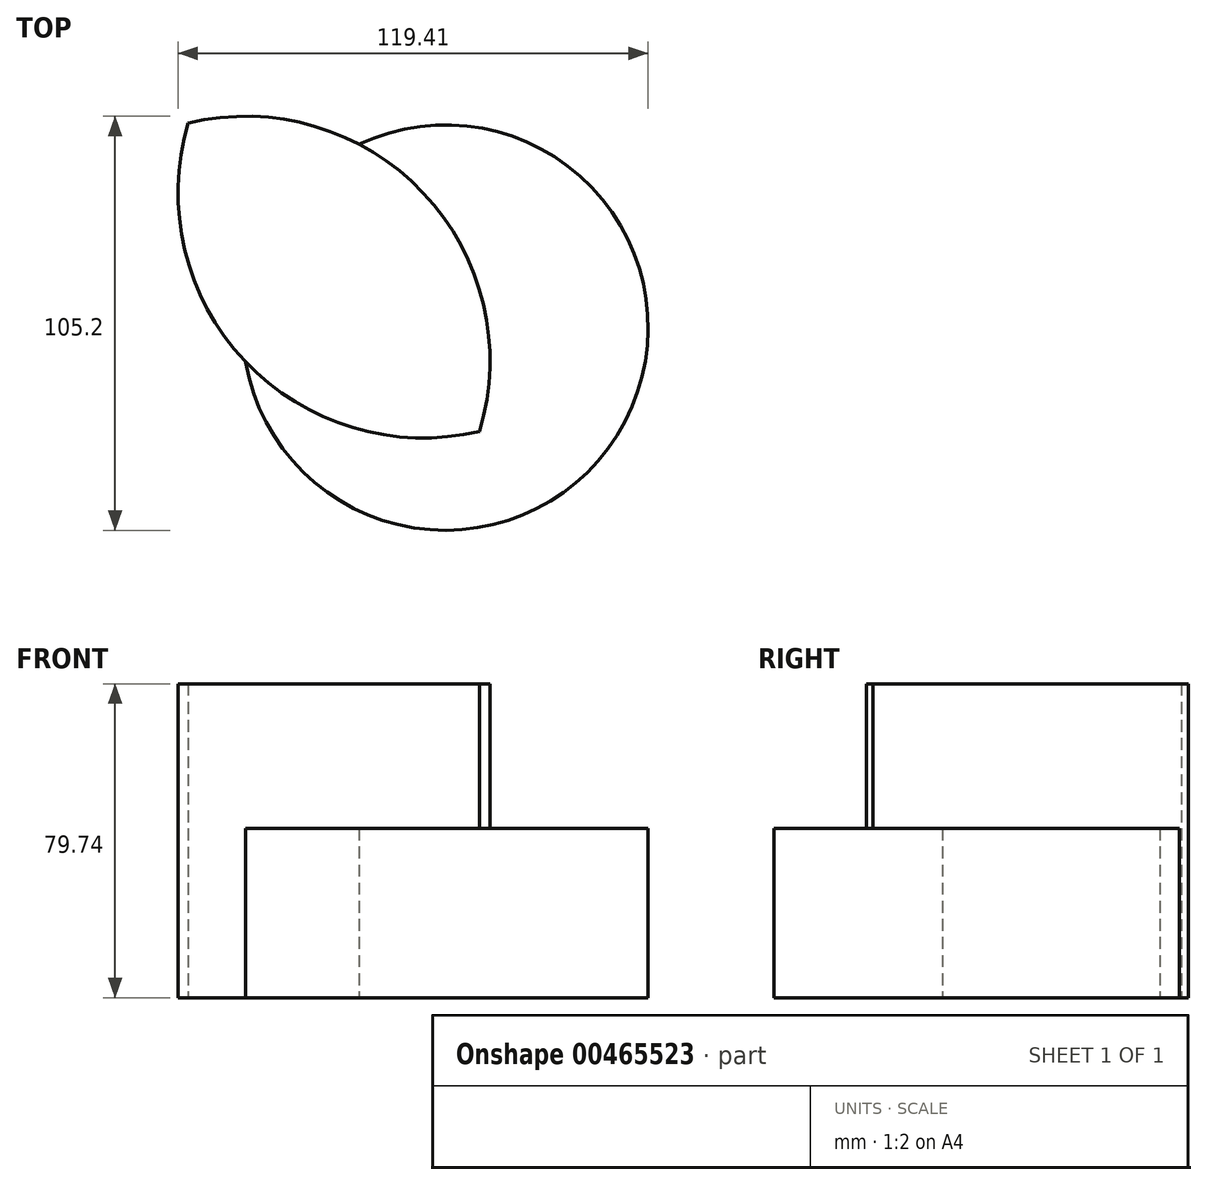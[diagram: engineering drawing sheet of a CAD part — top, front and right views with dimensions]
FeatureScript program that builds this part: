
annotation { "Feature Type Name" : "Feature", "Feature Type Description" : "" }
export const myFeature = defineFeature(function(context is Context, id is Id, definition is map)
    precondition{}
    {
        {
            var Q0;
            Q0=qCreatedBy(makeId("Top.planeOp"),FACE);
            var sketch = newSketch(context, id + "F0", { "sketchPlane" : qUnion([Q0])});
            skCircle(sketch, "E0", {"center": v(0, 0) * mm, "radius": 62.11 * mm});
            skCircle(sketch, "E1", {"center": v(45.15, 42.65) * mm, "radius": 62.28 * mm});
            skSolve(sketch);
        }
        {
            var Q0;
            {var subQ0=sQuery(id+"F0.wireOp",EDGE,"E1");var subQ1=sQuery(id+"F0.wireOp",EDGE,"E0");var subQ2=makeQuery(id+"F0.imprint","INTERSECT",VERTEX,{"disambiguationData":[OD(0.0)],"derivedFrom":[subQ1,subQ0]});Q0=makeQuery(id+"F0.imprint","IMPRINT",FACE,{"disambiguationData":[TD([[makeQuery(id+"F0.imprint","IMPRINT",EDGE,{"disambiguationData":[TD([[subQ2,1.0]])],"derivedFrom":subQ1}),1.0]])]});}
            extrude(context, id + "F1", {"entities" : qUnion([Q0]), "depth" : 79.74 * mm});
        }
        {
            var Q0;
            Q0=qCreatedBy(makeId("Top.planeOp"),FACE);
            var sketch = newSketch(context, id + "F2", { "sketchPlane" : qUnion([Q0])});
            skCircle(sketch, "E2", {"center": v(50.8, 8.4) * mm, "radius": 51.5 * mm});
            skPoint(sketch, "E2.first.point", {"position": v(0, 0) * mm});
            skPoint(sketch, "E2.second.point", {"position": v(61.18, -42.03) * mm});
            skPoint(sketch, "E2.third.point", {"position": v(75.08, 53.81) * mm});
            skSolve(sketch);
        }
        {
            var Q0;
            Q0 = qSketchRegion(id + "F2", true);
            extrude(context, id + "F3", {"entities" : qUnion([Q0]), "operationType" : NewBodyOperationType.ADD, "depth" : 43 * mm});
        }
    });
